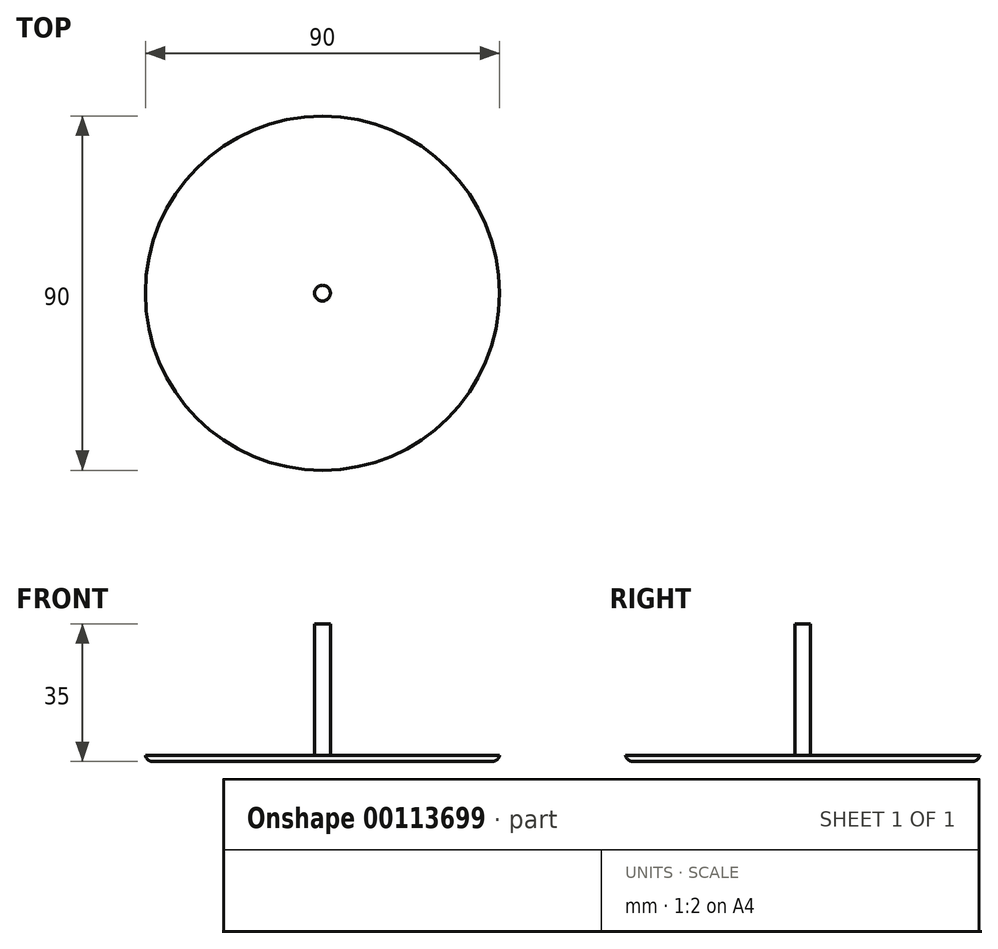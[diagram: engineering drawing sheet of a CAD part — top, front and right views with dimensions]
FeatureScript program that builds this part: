
annotation { "Feature Type Name" : "Feature", "Feature Type Description" : "" }
export const myFeature = defineFeature(function(context is Context, id is Id, definition is map)
    precondition{}
    {
        {
            var Q0;
            Q0=qCreatedBy(makeId("Top.planeOp"),FACE);
            var sketch = newSketch(context, id + "F0", { "sketchPlane" : qUnion([Q0])});
            skCircle(sketch, "E0", {"center": v(0, 0) * mm, "radius": 45 * mm});
            skCircle(sketch, "E1", {"center": v(0, 0) * mm, "radius": 2 * mm});
            skSolve(sketch);
        }
        {
            var Q0;
            Q0=makeQuery(id+"F0.imprint","IMPRINT",FACE,{"disambiguationData":[TD([[makeQuery(id+"F0.imprint","IMPRINT",EDGE,{"derivedFrom":sQuery(id+"F0.wireOp",EDGE,"E0")}),1.0]])]});
            extrude(context, id + "F1", {"entities" : qUnion([Q0]), "depth" : 1.5 * mm});
        }
        {
            var Q0;
            Q0=makeQuery(id+"F0.imprint","IMPRINT",FACE,{"disambiguationData":[TD([[makeQuery(id+"F0.imprint","IMPRINT",EDGE,{"derivedFrom":sQuery(id+"F0.wireOp",EDGE,"E1")}),1.0]])]});
            extrude(context, id + "F2", {"entities" : qUnion([Q0]), "operationType" : NewBodyOperationType.ADD, "depth" : 35 * mm});
        }
        {
            var Q0;
            Q0=makeQuery(id+"F1.opExtrude","CAP_EDGE",EDGE,{"disambiguationData":[OSD([sQuery(id+"F0.wireOp",EDGE,"E0")])],"isStart":true});
            fillet(context, id + "F3", {"entities" : qUnion([Q0]), "radius" : 2 * mm, "tangentPropagation" : true, "allowEdgeOverflow" : false});
        }
    });
